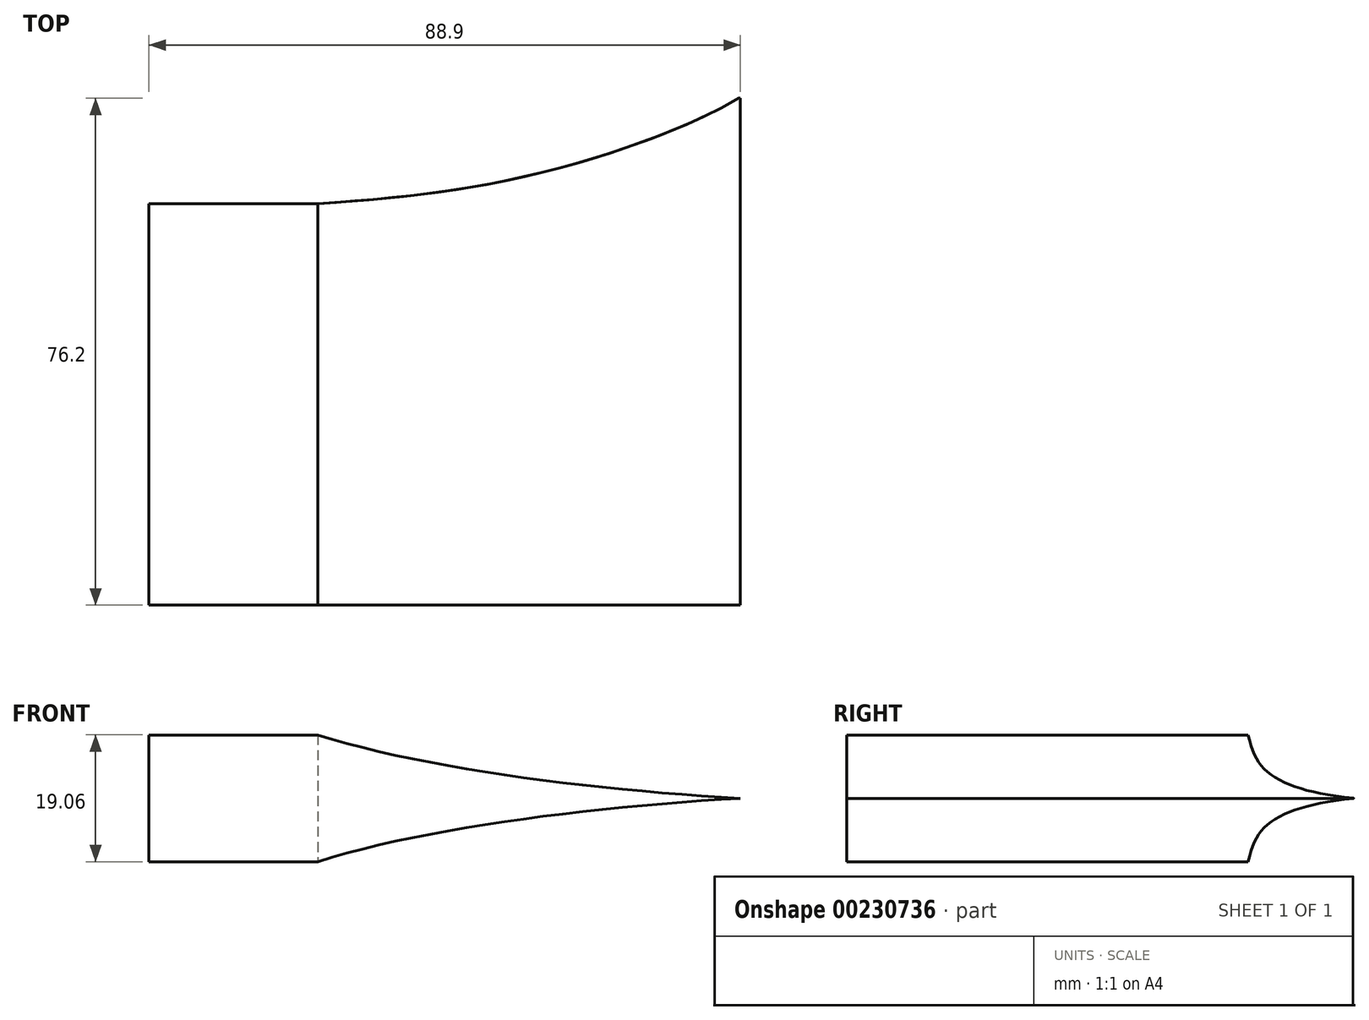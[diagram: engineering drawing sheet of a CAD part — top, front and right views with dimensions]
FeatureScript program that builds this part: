
annotation { "Feature Type Name" : "Feature", "Feature Type Description" : "" }
export const myFeature = defineFeature(function(context is Context, id is Id, definition is map)
    precondition{}
    {
        {
            var Q0;
            Q0=qCreatedBy(makeId("Front.planeOp"),FACE);
            var sketch = newSketch(context, id + "F0", { "sketchPlane" : qUnion([Q0])});
            skLineSegment(sketch, "E0", {"start": v(-37.29, 0) * mm, "end": v(88.9, 0) * mm, "construction": true});
            skLineSegment(sketch, "E1", {"start": v(0, 0) * mm, "end": v(0, 9.53) * mm});
            skLineSegment(sketch, "E2", {"start": v(0, 9.53) * mm, "end": v(25.4, 9.53) * mm});
            skFitSpline(sketch, "E3", {"points": [v(25.4, 9.53) * mm, v(88.9, 0) * mm], "startDerivative": vector(47.97, -15.3) * mm, "endDerivative": vector(66.25, -3.73) * mm});
            skFitSpline(sketch, "E4.MirrorCS", {"points": [v(25.4, -9.53) * mm, v(88.9, 0) * mm], "startDerivative": vector(47.97, 15.3) * mm, "endDerivative": vector(66.25, 3.73) * mm});
            skLineSegment(sketch, "E5.MirrorCS", {"start": v(0, 0) * mm, "end": v(0, -9.53) * mm});
            skLineSegment(sketch, "E6.MirrorCS", {"start": v(0, -9.53) * mm, "end": v(25.4, -9.53) * mm});
            skSolve(sketch);
        }
        {
            var Q0;
            Q0=makeQuery(id+"F0.imprint","IMPRINT",FACE,{"disambiguationData":[TD([[makeQuery(id+"F0.imprint","IMPRINT",EDGE,{"derivedFrom":sQuery(id+"F0.wireOp",EDGE,"E1")}),-1.0]])]});
            extrude(context, id + "F1", {"entities" : qUnion([Q0]), "depth" : 76.2 * mm});
        }
        {
            var Q0;
            Q0=makeQuery(id+"F1.opExtrude","SWEPT_FACE",FACE,{"disambiguationData":[OSD([sQuery(id+"F0.wireOp",EDGE,"E6.MirrorCS")])]});
            var sketch = newSketch(context, id + "F2", { "sketchPlane" : qUnion([Q0])});
            skLineSegment(sketch, "E7", {"start": v(0, 15.88) * mm, "end": v(0, -11.25) * mm});
            skLineSegment(sketch, "E8", {"start": v(0, -11.25) * mm, "end": v(102, -11.25) * mm});
            skLineSegment(sketch, "E9", {"start": v(0, 15.88) * mm, "end": v(25.4, 15.88) * mm});
            skFitSpline(sketch, "E10", {"points": [v(25.4, 15.88) * mm, v(54.94, 12.1) * mm, v(88.6, 0) * mm, v(102, -11.25) * mm], "startDerivative": vector(80.8, -6.2) * mm, "endDerivative": vector(41.39, -43.11) * mm});
            skSolve(sketch);
        }
        {
            var Q0;
            Q0 = qSketchRegion(id + "F2", true);
            extrude(context, id + "F3", {"entities" : qUnion([Q0]), "operationType" : NewBodyOperationType.REMOVE, "endBound" : BoundingType.THROUGH_ALL, "oppositeDirection" : true, "depth" : 25.4 * mm});
        }
    });
